# Revit family: Sanitary_Taps&Mixers_Toto_T27S51E-Standard-S-Touchless-Faucet
name_source: partatom
category: Plumbing Fixtures
units: mm (PartAtom-declared; Revit-internal decimal feet)

## family parameters
Cut with Voids When Loaded = No
Host = Face
OmniClass Number = 23.45.55.14
OmniClass Title = Single Faucets
Part Type = Normal
Room Calculation Point = No
Round Connector Dimension = Use Diameter
Shared = No

## types (4) — shared parameters
Ambient Temperature = 32-104°F (0-40°C)
Apparent Load = 0 VA
Assembly Code = D2010
Chilled Water Connection Diameter = 1"
Default Elevation = 0' - 0"
Depth = 0' - 5 31/32"
Description = Standard-S Touchless Faucet
Edition number = 1
Height = 0' - 6 1/2"
Hot Water Connection Diameter = 1"
Humidity = Max. 90% RH
Inlet Temperature Range = 39-110°F (4-43°C)
Keynote = 15410
Manufacturer = TOTO USA Inc.
Maximum Water Pressure (static) = 80.00 psi
Minimum Water Pressure (flowing) = 15.00 psi
Model = T27S51E
Number of Poles = 1
Power Factor = 1
Product Material = Toto - Steel - Zinc Diecast
URL = http://www.totousa.com
Voltage = 0 V
Water Supply Connection = Connects to TOTO touchless faucet controller
Width = 0' - 1 15/16"

## per-type parameters (varying)
| type | Duration | Flow Rate GPC (by controller) | Flow Rate GPM (by controller) | Mode |
| TLE27001U2#CP | 20 sec | 0.12 gpc | 0 GPM | On-demand |
| TLE27002U1#CP | 10 sec | 0.08 gpc | 1 GPM | On-demand |
| TLE27002U3#CP | 20 sec | 0.17 gpc | 1 GPM | Continuous |
| TLE27003U1#CP | 10 sec | 0.18 gpc | 1 GPM | On-demand |

## geometry (parser evidence)
native form markers: Sweep x2
no freeform markers — native parametric forms only
